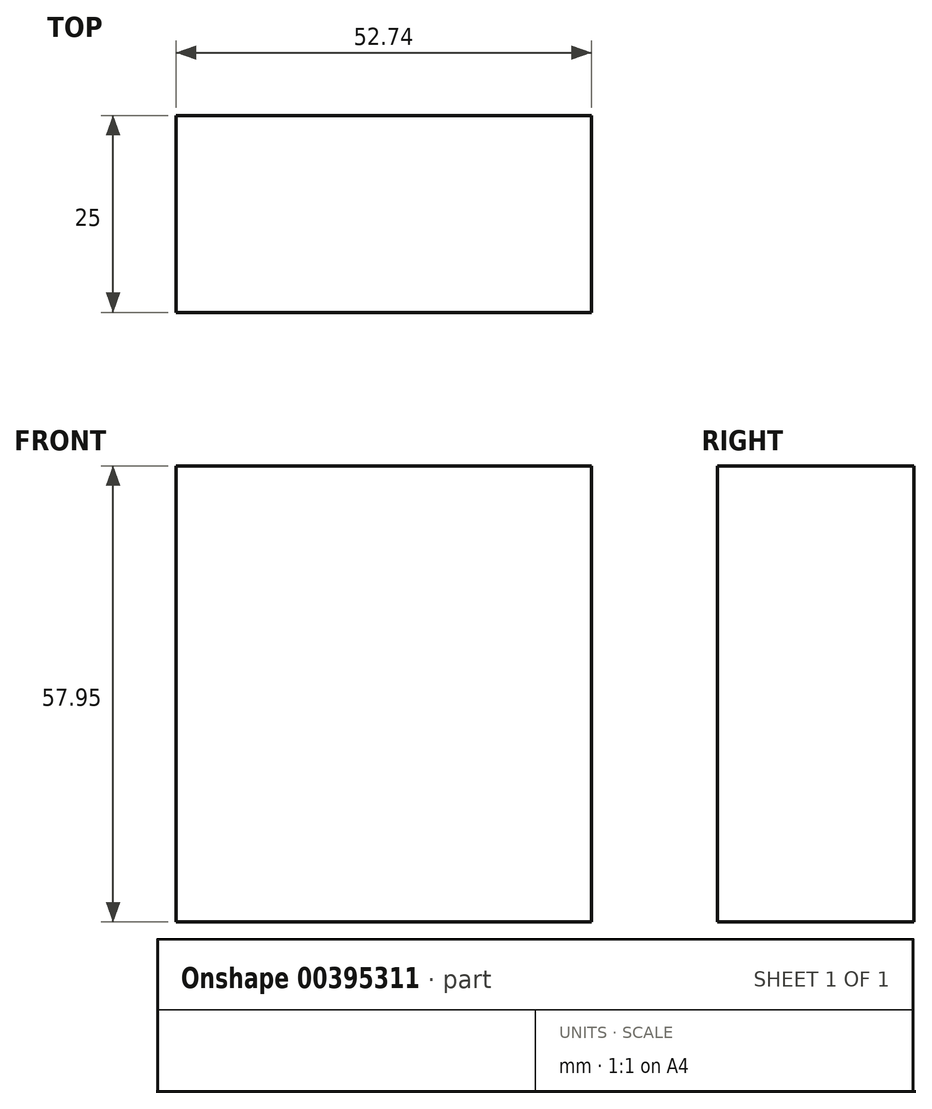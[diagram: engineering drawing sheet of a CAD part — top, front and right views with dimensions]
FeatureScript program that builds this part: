
annotation { "Feature Type Name" : "Feature", "Feature Type Description" : "" }
export const myFeature = defineFeature(function(context is Context, id is Id, definition is map)
    precondition{}
    {
        {
            var Q0;
            Q0=qCreatedBy(makeId("Front.planeOp"),FACE);
            var sketch = newSketch(context, id + "F0", { "sketchPlane" : qUnion([Q0])});
            skLineSegment(sketch, "E0.bottom", {"start": v(-129.5, 0) * mm, "end": v(-76.77, 0) * mm});
            skLineSegment(sketch, "E0.top", {"start": v(-129.5, 57.95) * mm, "end": v(-76.77, 57.95) * mm});
            skLineSegment(sketch, "E0.left", {"start": v(-129.5, 0) * mm, "end": v(-129.5, 57.95) * mm});
            skLineSegment(sketch, "E0.right", {"start": v(-76.77, 0) * mm, "end": v(-76.77, 57.95) * mm});
            skPoint(sketch, "E0.middle", {"position": v(-103.14, 28.97) * mm});
            skSolve(sketch);
        }
        {
            var Q0;
            Q0=makeQuery(id+"F0.imprint","IMPRINT",FACE,{"disambiguationData":[TD([[makeQuery(id+"F0.imprint","IMPRINT",EDGE,{"derivedFrom":sQuery(id+"F0.wireOp",EDGE,"E0.bottom")}),1.0]])]});
            extrude(context, id + "F1", {"entities" : qUnion([Q0]), "depth" : 25 * mm});
        }
    });
